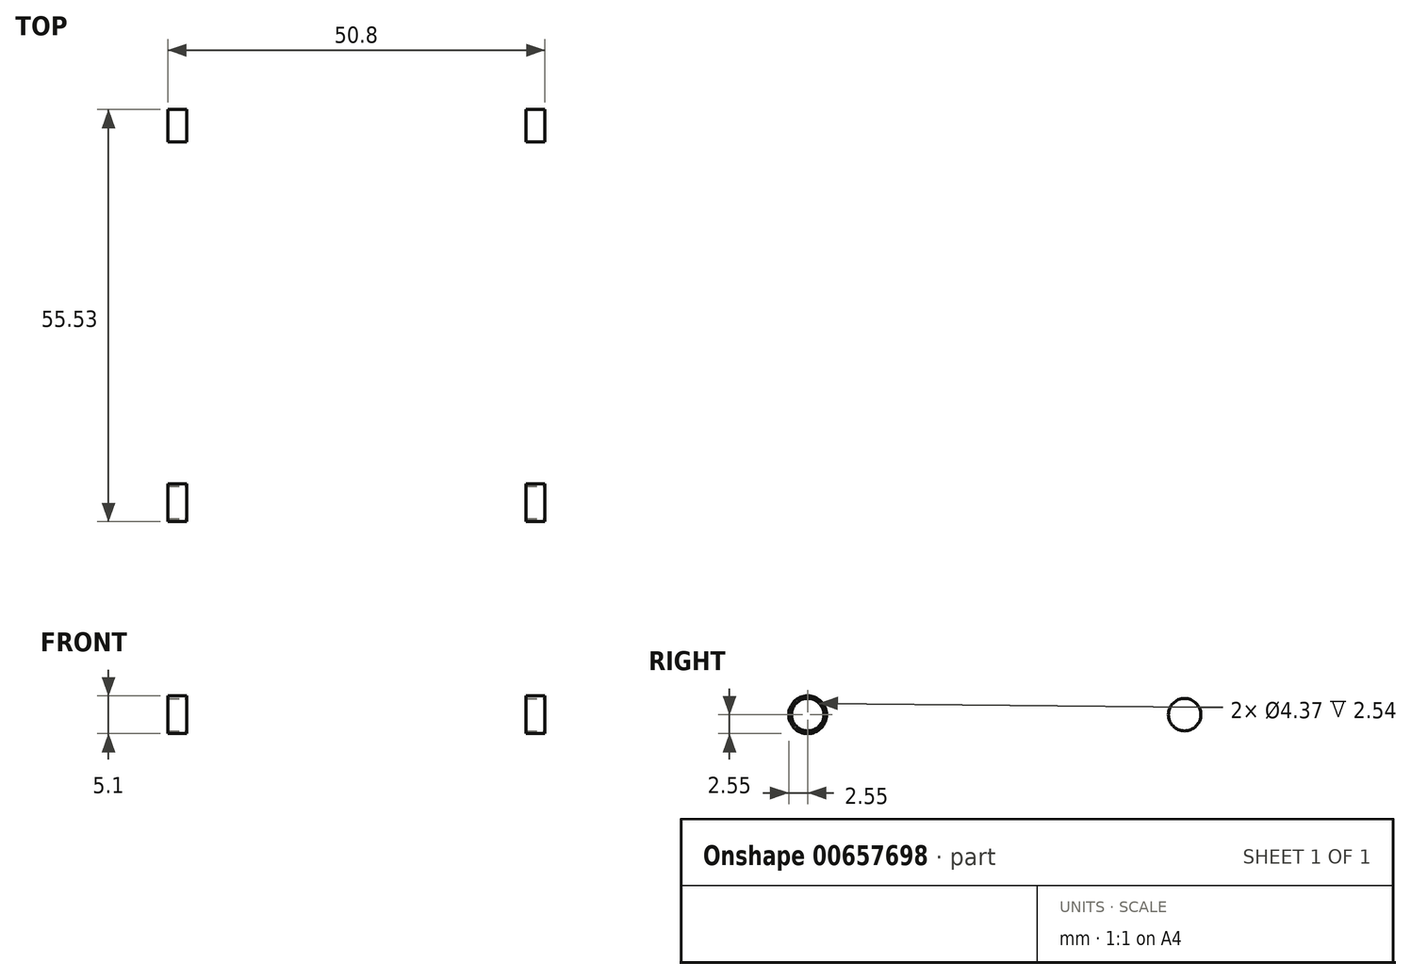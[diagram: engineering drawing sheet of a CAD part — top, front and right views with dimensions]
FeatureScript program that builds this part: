
annotation { "Feature Type Name" : "Feature", "Feature Type Description" : "" }
export const myFeature = defineFeature(function(context is Context, id is Id, definition is map)
    precondition{}
    {
        {
            var Q0;
            Q0=qCreatedBy(makeId("Front.planeOp"),FACE);
            var sketch = newSketch(context, id + "F0", { "sketchPlane" : qUnion([Q0])});
            skLineSegment(sketch, "E0.bottom", {"start": v(0, 0) * mm, "end": v(50.8, 0) * mm});
            skLineSegment(sketch, "E0.top", {"start": v(0, 25.4) * mm, "end": v(50.8, 25.4) * mm});
            skLineSegment(sketch, "E0.left", {"start": v(0, 0) * mm, "end": v(0, 25.4) * mm});
            skLineSegment(sketch, "E0.right", {"start": v(50.8, 0) * mm, "end": v(50.8, 25.4) * mm});
            skLineSegment(sketch, "E1.bottom", {"start": v(2.54, 22.86) * mm, "end": v(48.26, 22.86) * mm});
            skLineSegment(sketch, "E1.top", {"start": v(2.54, 2.54) * mm, "end": v(48.26, 2.54) * mm});
            skLineSegment(sketch, "E1.left", {"start": v(2.54, 22.86) * mm, "end": v(2.54, 2.54) * mm});
            skLineSegment(sketch, "E1.right", {"start": v(48.26, 22.86) * mm, "end": v(48.26, 2.54) * mm});
            skSolve(sketch);
        }
        {
            var Q0;
            Q0=makeQuery(id+"F0.imprint","IMPRINT",FACE,{"disambiguationData":[TD([[makeQuery(id+"F0.imprint","IMPRINT",EDGE,{"derivedFrom":sQuery(id+"F0.wireOp",EDGE,"E0.bottom")}),1.0]])]});
            extrude(context, id + "F1", {"entities" : qUnion([Q0]), "depth" : 101.6 * mm, "offsetDistance" : 25.4 * mm});
        }
        {
            var Q0;
            Q0=makeQuery(id+"F1.opExtrude","SWEPT_FACE",FACE,{"disambiguationData":[OSD([sQuery(id+"F0.wireOp",EDGE,"E0.right")])]});
            var sketch = newSketch(context, id + "F2", { "sketchPlane" : qUnion([Q0])});
            skLineSegment(sketch, "E2", {"start": v(0, 12.7) * mm, "end": v(-101.6, 12.7) * mm});
            skCircle(sketch, "E3", {"center": v(-12.7, 12.7) * mm, "radius": 2.18 * mm});
            skCircle(sketch, "E4", {"center": v(-38.1, 12.7) * mm, "radius": 2.18 * mm});
            skCircle(sketch, "E5", {"center": v(-63.5, 12.7) * mm, "radius": 2.18 * mm});
            skCircle(sketch, "E6", {"center": v(-88.9, 12.7) * mm, "radius": 2.18 * mm});
            skCircle(sketch, "E7", {"center": v(-88.9, 12.7) * mm, "radius": 2.55 * mm});
            skCircle(sketch, "E8", {"center": v(-63.5, 12.7) * mm, "radius": 2.55 * mm});
            skCircle(sketch, "E9", {"center": v(-38.1, 12.7) * mm, "radius": 2.55 * mm});
            skCircle(sketch, "E10", {"center": v(-12.7, 12.7) * mm, "radius": 2.55 * mm});
            skSolve(sketch);
        }
        {
            var Q0;
            {var subQ0=sQuery(id+"F2.wireOp",EDGE,"E6");var subQ1=sQuery(id+"F2.wireOp",EDGE,"E2");var subQ2=makeQuery(id+"F2.imprint","INTERSECT",VERTEX,{"disambiguationData":[OD(0.0)],"derivedFrom":[subQ1,subQ0]});Q0=makeQuery(id+"F2.imprint","IMPRINT",FACE,{"disambiguationData":[TD([[makeQuery(id+"F2.imprint","IMPRINT",EDGE,{"disambiguationData":[TD([[subQ2,-1.0]])],"derivedFrom":subQ1}),1.0]])]});}
            var Q1;
            {var subQ0=sQuery(id+"F2.wireOp",EDGE,"E5");var subQ1=sQuery(id+"F2.wireOp",EDGE,"E2");var subQ2=makeQuery(id+"F2.imprint","INTERSECT",VERTEX,{"disambiguationData":[OD(0.0)],"derivedFrom":[subQ1,subQ0]});Q1=makeQuery(id+"F2.imprint","IMPRINT",FACE,{"disambiguationData":[TD([[makeQuery(id+"F2.imprint","IMPRINT",EDGE,{"disambiguationData":[TD([[subQ2,-1.0]])],"derivedFrom":subQ1}),1.0]])]});}
            var Q2;
            {var subQ0=sQuery(id+"F2.wireOp",EDGE,"E5");var subQ1=sQuery(id+"F2.wireOp",EDGE,"E2");var subQ2=makeQuery(id+"F2.imprint","INTERSECT",VERTEX,{"disambiguationData":[OD(0.0)],"derivedFrom":[subQ1,subQ0]});Q2=makeQuery(id+"F2.imprint","IMPRINT",FACE,{"disambiguationData":[TD([[makeQuery(id+"F2.imprint","IMPRINT",EDGE,{"disambiguationData":[TD([[subQ2,-1.0]])],"derivedFrom":subQ1}),-1.0]])]});}
            var Q3;
            {var subQ0=sQuery(id+"F2.wireOp",EDGE,"E4");var subQ1=sQuery(id+"F2.wireOp",EDGE,"E2");var subQ2=makeQuery(id+"F2.imprint","INTERSECT",VERTEX,{"disambiguationData":[OD(0.0)],"derivedFrom":[subQ1,subQ0]});Q3=makeQuery(id+"F2.imprint","IMPRINT",FACE,{"disambiguationData":[TD([[makeQuery(id+"F2.imprint","IMPRINT",EDGE,{"disambiguationData":[TD([[subQ2,-1.0]])],"derivedFrom":subQ1}),1.0]])]});}
            var Q4;
            {var subQ0=sQuery(id+"F2.wireOp",EDGE,"E4");var subQ1=sQuery(id+"F2.wireOp",EDGE,"E2");var subQ2=makeQuery(id+"F2.imprint","INTERSECT",VERTEX,{"disambiguationData":[OD(0.0)],"derivedFrom":[subQ1,subQ0]});Q4=makeQuery(id+"F2.imprint","IMPRINT",FACE,{"disambiguationData":[TD([[makeQuery(id+"F2.imprint","IMPRINT",EDGE,{"disambiguationData":[TD([[subQ2,-1.0]])],"derivedFrom":subQ1}),-1.0]])]});}
            var Q5;
            {var subQ0=sQuery(id+"F2.wireOp",EDGE,"E3");var subQ1=sQuery(id+"F2.wireOp",EDGE,"E2");var subQ2=makeQuery(id+"F2.imprint","INTERSECT",VERTEX,{"disambiguationData":[OD(0.0)],"derivedFrom":[subQ1,subQ0]});Q5=makeQuery(id+"F2.imprint","IMPRINT",FACE,{"disambiguationData":[TD([[makeQuery(id+"F2.imprint","IMPRINT",EDGE,{"disambiguationData":[TD([[subQ2,-1.0]])],"derivedFrom":subQ1}),1.0]])]});}
            var Q6;
            {var subQ0=sQuery(id+"F2.wireOp",EDGE,"E3");var subQ1=sQuery(id+"F2.wireOp",EDGE,"E2");var subQ2=makeQuery(id+"F2.imprint","INTERSECT",VERTEX,{"disambiguationData":[OD(0.0)],"derivedFrom":[subQ1,subQ0]});Q6=makeQuery(id+"F2.imprint","IMPRINT",FACE,{"disambiguationData":[TD([[makeQuery(id+"F2.imprint","IMPRINT",EDGE,{"disambiguationData":[TD([[subQ2,-1.0]])],"derivedFrom":subQ1}),-1.0]])]});}
            var Q7;
            {var subQ0=sQuery(id+"F2.wireOp",EDGE,"E6");var subQ1=sQuery(id+"F2.wireOp",EDGE,"E2");var subQ2=makeQuery(id+"F2.imprint","INTERSECT",VERTEX,{"disambiguationData":[OD(0.0)],"derivedFrom":[subQ1,subQ0]});Q7=makeQuery(id+"F2.imprint","IMPRINT",FACE,{"disambiguationData":[TD([[makeQuery(id+"F2.imprint","IMPRINT",EDGE,{"disambiguationData":[TD([[subQ2,-1.0]])],"derivedFrom":subQ1}),-1.0]])]});}
            var Q8;
            {var subQ0=sQuery(id+"F2.wireOp",EDGE,"E10");var subQ1=sQuery(id+"F2.wireOp",EDGE,"E2");var subQ2=makeQuery(id+"F2.imprint","INTERSECT",VERTEX,{"disambiguationData":[OD(0.0)],"derivedFrom":[subQ1,subQ0]});Q8=makeQuery(id+"F2.imprint","IMPRINT",FACE,{"disambiguationData":[TD([[makeQuery(id+"F2.imprint","IMPRINT",EDGE,{"disambiguationData":[TD([[subQ2,-1.0]])],"derivedFrom":subQ1}),1.0]])]});}
            var Q9;
            {var subQ0=sQuery(id+"F2.wireOp",EDGE,"E10");var subQ1=sQuery(id+"F2.wireOp",EDGE,"E2");var subQ2=makeQuery(id+"F2.imprint","INTERSECT",VERTEX,{"disambiguationData":[OD(0.0)],"derivedFrom":[subQ1,subQ0]});Q9=makeQuery(id+"F2.imprint","IMPRINT",FACE,{"disambiguationData":[TD([[makeQuery(id+"F2.imprint","IMPRINT",EDGE,{"disambiguationData":[TD([[subQ2,-1.0]])],"derivedFrom":subQ1}),-1.0]])]});}
            var Q10;
            {var subQ0=sQuery(id+"F2.wireOp",EDGE,"E9");var subQ1=sQuery(id+"F2.wireOp",EDGE,"E2");var subQ2=makeQuery(id+"F2.imprint","INTERSECT",VERTEX,{"disambiguationData":[OD(0.0)],"derivedFrom":[subQ1,subQ0]});Q10=makeQuery(id+"F2.imprint","IMPRINT",FACE,{"disambiguationData":[TD([[makeQuery(id+"F2.imprint","IMPRINT",EDGE,{"disambiguationData":[TD([[subQ2,-1.0]])],"derivedFrom":subQ1}),1.0]])]});}
            var Q11;
            {var subQ0=sQuery(id+"F2.wireOp",EDGE,"E9");var subQ1=sQuery(id+"F2.wireOp",EDGE,"E2");var subQ2=makeQuery(id+"F2.imprint","INTERSECT",VERTEX,{"disambiguationData":[OD(0.0)],"derivedFrom":[subQ1,subQ0]});Q11=makeQuery(id+"F2.imprint","IMPRINT",FACE,{"disambiguationData":[TD([[makeQuery(id+"F2.imprint","IMPRINT",EDGE,{"disambiguationData":[TD([[subQ2,-1.0]])],"derivedFrom":subQ1}),-1.0]])]});}
            var Q12;
            {var subQ0=sQuery(id+"F2.wireOp",EDGE,"E7");var subQ1=sQuery(id+"F2.wireOp",EDGE,"E2");var subQ2=makeQuery(id+"F2.imprint","INTERSECT",VERTEX,{"disambiguationData":[OD(0.0)],"derivedFrom":[subQ1,subQ0]});Q12=makeQuery(id+"F2.imprint","IMPRINT",FACE,{"disambiguationData":[TD([[makeQuery(id+"F2.imprint","IMPRINT",EDGE,{"disambiguationData":[TD([[subQ2,-1.0]])],"derivedFrom":subQ1}),1.0]])]});}
            var Q13;
            {var subQ0=sQuery(id+"F2.wireOp",EDGE,"E7");var subQ1=sQuery(id+"F2.wireOp",EDGE,"E2");var subQ2=makeQuery(id+"F2.imprint","INTERSECT",VERTEX,{"disambiguationData":[OD(0.0)],"derivedFrom":[subQ1,subQ0]});Q13=makeQuery(id+"F2.imprint","IMPRINT",FACE,{"disambiguationData":[TD([[makeQuery(id+"F2.imprint","IMPRINT",EDGE,{"disambiguationData":[TD([[subQ2,-1.0]])],"derivedFrom":subQ1}),-1.0]])]});}
            var Q14;
            {var subQ0=sQuery(id+"F2.wireOp",EDGE,"E8");var subQ1=sQuery(id+"F2.wireOp",EDGE,"E2");var subQ2=makeQuery(id+"F2.imprint","INTERSECT",VERTEX,{"disambiguationData":[OD(0.0)],"derivedFrom":[subQ1,subQ0]});Q14=makeQuery(id+"F2.imprint","IMPRINT",FACE,{"disambiguationData":[TD([[makeQuery(id+"F2.imprint","IMPRINT",EDGE,{"disambiguationData":[TD([[subQ2,-1.0]])],"derivedFrom":subQ1}),1.0]])]});}
            var Q15;
            {var subQ0=sQuery(id+"F2.wireOp",EDGE,"E8");var subQ1=sQuery(id+"F2.wireOp",EDGE,"E2");var subQ2=makeQuery(id+"F2.imprint","INTERSECT",VERTEX,{"disambiguationData":[OD(0.0)],"derivedFrom":[subQ1,subQ0]});Q15=makeQuery(id+"F2.imprint","IMPRINT",FACE,{"disambiguationData":[TD([[makeQuery(id+"F2.imprint","IMPRINT",EDGE,{"disambiguationData":[TD([[subQ2,-1.0]])],"derivedFrom":subQ1}),-1.0]])]});}
            extrude(context, id + "F3", {"entities" : qUnion([Q0, Q1, Q2, Q3, Q4, Q5, Q6, Q7, Q8, Q9, Q10, Q11, Q12, Q13, Q14, Q15]), "operationType" : NewBodyOperationType.REMOVE, "oppositeDirection" : true, "depth" : 127 * mm, "offsetDistance" : 25.4 * mm});
        }
    });
